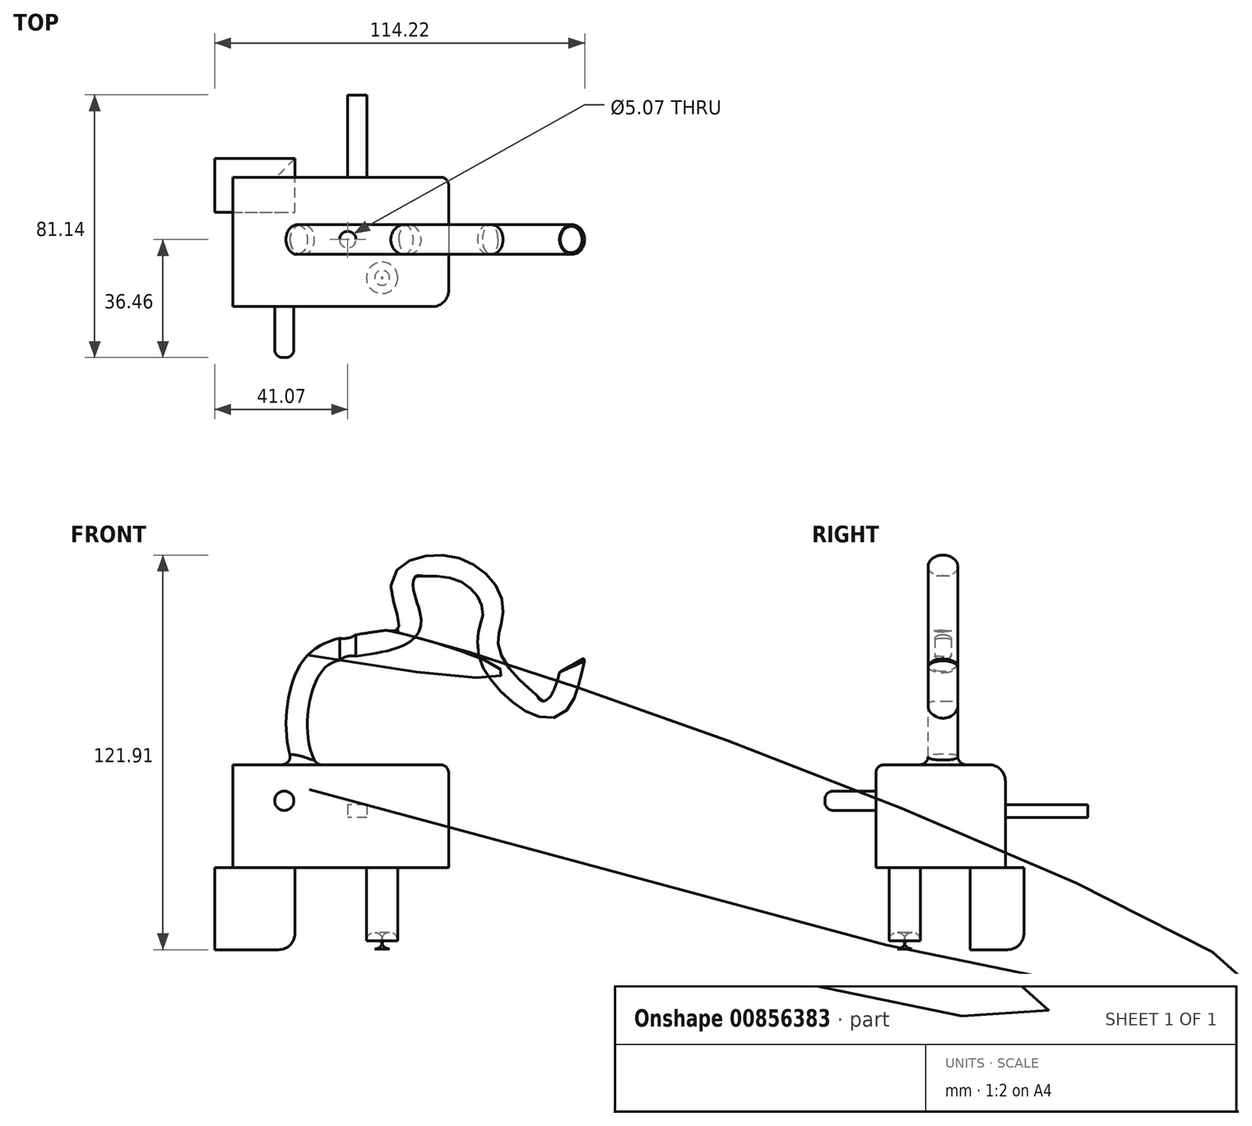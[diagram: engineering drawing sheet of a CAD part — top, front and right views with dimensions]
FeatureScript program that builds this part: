
annotation { "Feature Type Name" : "Feature", "Feature Type Description" : "" }
export const myFeature = defineFeature(function(context is Context, id is Id, definition is map)
    precondition{}
    {
        {
            var Q0;
            Q0=qCreatedBy(makeId("Top.planeOp"),FACE);
            var sketch = newSketch(context, id + "F0", { "sketchPlane" : qUnion([Q0])});
            skLineSegment(sketch, "E0.bottom", {"start": v(-35.49, 19.28) * mm, "end": v(31.16, 19.28) * mm});
            skLineSegment(sketch, "E0.top", {"start": v(-35.49, -20.72) * mm, "end": v(31.16, -20.72) * mm});
            skLineSegment(sketch, "E0.left", {"start": v(-35.49, 19.28) * mm, "end": v(-35.49, -20.72) * mm});
            skLineSegment(sketch, "E0.right", {"start": v(31.16, 19.28) * mm, "end": v(31.16, -20.72) * mm});
            skSolve(sketch);
        }
        {
            var Q0;
            Q0 = qSketchRegion(id + "F0", true);
            extrude(context, id + "F1", {"entities" : qUnion([Q0]), "depth" : 31.75 * mm, "offsetDistance" : 25.4 * mm});
        }
        {
            var Q0;
            Q0=makeQuery(id+"F1.opExtrude","SWEPT_FACE",FACE,{"disambiguationData":[OSD([sQuery(id+"F0.wireOp",EDGE,"E0.top")])]});
            var sketch = newSketch(context, id + "F2", { "sketchPlane" : qUnion([Q0])});
            skCircle(sketch, "E1", {"center": v(-19.62, 20.6) * mm, "radius": 2.98 * mm});
            skSolve(sketch);
        }
        {
            var Q0;
            Q0 = qSketchRegion(id + "F2", true);
            extrude(context, id + "F3", {"entities" : qUnion([Q0]), "operationType" : NewBodyOperationType.ADD, "depth" : 15.75 * mm, "offsetDistance" : 25.4 * mm});
        }
        {
            var Q0;
            Q0=makeQuery(id+"F1.opExtrude","SWEPT_EDGE",EDGE,{"disambiguationData":[OSD([sQuery(id+"F0.wireOp",EDGE,"E0.top"),sQuery(id+"F0.wireOp",EDGE,"E0.right")])]});
            fillet(context, id + "F4", {"entities" : qUnion([Q0]), "radius" : 5.08 * mm, "tangentPropagation" : true, "allowEdgeOverflow" : false});
        }
        {
            var Q0;
            Q0=makeQuery(id+"F1.opExtrude","CAP_FACE",FACE,{"disambiguationData":[OSD([sQuery(id+"F0.wireOp",EDGE,"E0.bottom"),sQuery(id+"F0.wireOp",EDGE,"E0.top"),sQuery(id+"F0.wireOp",EDGE,"E0.left"),sQuery(id+"F0.wireOp",EDGE,"E0.right")])],"isStart":true});
            var sketch = newSketch(context, id + "F5", { "sketchPlane" : qUnion([Q0])});
            skCircle(sketch, "E2", {"center": v(0, 0) * mm, "radius": 4.6 * mm});
            skSolve(sketch);
        }
        {
            var Q0;
            Q0=qCreatedBy(makeId("Front.planeOp"),FACE);
            var sketch = newSketch(context, id + "F6", { "sketchPlane" : qUnion([Q0])});
            skFitSpline(sketch, "E3", {"points": [v(0, 0) * mm, v(8.49, 13.84) * mm, v(-6.4, 24.07) * mm, v(-15.47, 40.82) * mm, v(-10.35, 62.45) * mm, v(5, 68.96) * mm, v(18.5, 74.78) * mm, v(17.56, 88.5) * mm, v(33.14, 92.22) * mm, v(44.3, 80.6) * mm, v(44.3, 65) * mm, v(61.98, 49.89) * mm, v(69.43, 62.68) * mm], "startDerivative": vector(179.85, 187.23) * mm, "endDerivative": vector(60.45, 239.3) * mm});
            skSolve(sketch);
        }
        {
            var Q0;
            Q0 = qSketchRegion(id + "F5", true);
            var Q1;
            Q1 = qConstructionFilter(qBodyType(qCreatedBy(id + "F6" ,EDGE), BodyType.WIRE), ConstructionObject.NO);
            sweep(context, id + "F7", {"operationType" : NewBodyOperationType.ADD, "profiles" : qUnion([Q0]), "path" : qUnion([Q1])});
        }
        {
            var Q0;
            Q0=makeQuery(id+"F1.opExtrude","SWEPT_FACE",FACE,{"disambiguationData":[OSD([sQuery(id+"F0.wireOp",EDGE,"E0.bottom")])]});
            var sketch = newSketch(context, id + "F8", { "sketchPlane" : qUnion([Q0])});
            skLineSegment(sketch, "E4.bottom", {"start": v(-5.84, 19.34) * mm, "end": v(0, 19.34) * mm});
            skLineSegment(sketch, "E4.top", {"start": v(-5.84, 15.39) * mm, "end": v(0, 15.39) * mm});
            skLineSegment(sketch, "E4.left", {"start": v(-5.84, 19.34) * mm, "end": v(-5.84, 15.39) * mm});
            skLineSegment(sketch, "E4.right", {"start": v(0, 19.34) * mm, "end": v(0, 15.39) * mm});
            skSolve(sketch);
        }
        {
            var Q0;
            Q0 = qSketchRegion(id + "F8", true);
            extrude(context, id + "F9", {"entities" : qUnion([Q0]), "operationType" : NewBodyOperationType.ADD, "depth" : 25.4 * mm, "offsetDistance" : 25.4 * mm});
        }
        {
            var Q0;
            Q0=makeQuery(id+"F1.opExtrude","CAP_EDGE",EDGE,{"disambiguationData":[OSD([sQuery(id+"F0.wireOp",EDGE,"E0.bottom")])],"isStart":false});
            fillet(context, id + "F10", {"entities" : qUnion([Q0]), "radius" : 5.08 * mm, "tangentPropagation" : true, "allowEdgeOverflow" : false});
        }
        {
            var Q0;
            Q0=makeQuery(id+"F7.opSweep","CAP_EDGE",EDGE,{"disambiguationData":[OSD([sQuery(id+"F5.wireOp",EDGE,"E2"),sQuery(id+"F6.wireOp",VERTEX,"E3.end")])],"isStart":false});
            fillet(context, id + "F11", {"entities" : qUnion([Q0]), "radius" : 0.5 * mm, "tangentPropagation" : true, "allowEdgeOverflow" : false});
        }
        {
            var Q0;
            Q0=makeQuery(id+"F1.opExtrude","CAP_FACE",FACE,{"disambiguationData":[OSD([sQuery(id+"F0.wireOp",EDGE,"E0.bottom"),sQuery(id+"F0.wireOp",EDGE,"E0.top"),sQuery(id+"F0.wireOp",EDGE,"E0.left"),sQuery(id+"F0.wireOp",EDGE,"E0.right")])],"isStart":true});
            var sketch = newSketch(context, id + "F12", { "sketchPlane" : qUnion([Q0])});
            skLineSegment(sketch, "E5.bottom", {"start": v(-41.07, -8.38) * mm, "end": v(-16.3, -8.38) * mm});
            skLineSegment(sketch, "E5.top", {"start": v(-41.07, -25.02) * mm, "end": v(-16.3, -25.02) * mm});
            skLineSegment(sketch, "E5.left", {"start": v(-41.07, -8.38) * mm, "end": v(-41.07, -25.02) * mm});
            skLineSegment(sketch, "E5.right", {"start": v(-16.3, -8.38) * mm, "end": v(-16.3, -25.02) * mm});
            skSolve(sketch);
        }
        {
            var Q0;
            Q0 = qSketchRegion(id + "F12", true);
            extrude(context, id + "F13", {"entities" : qUnion([Q0]), "operationType" : NewBodyOperationType.ADD, "depth" : 25.4 * mm, "offsetDistance" : 25.4 * mm});
        }
        {
            var Q0;
            Q0=qCreatedBy(makeId("Top.planeOp"),FACE);
            var sketch = newSketch(context, id + "F14", { "sketchPlane" : qUnion([Q0])});
            skCircle(sketch, "E6", {"center": v(10.6, -11.82) * mm, "radius": 4.84 * mm});
            skSolve(sketch);
        }
        {
            var Q0;
            Q0=makeQuery(id+"F14.imprint","IMPRINT",FACE,{"disambiguationData":[TD([[makeQuery(id+"F14.imprint","IMPRINT",EDGE,{"derivedFrom":sQuery(id+"F14.wireOp",EDGE,"E6")}),1.0]])]});
            extrude(context, id + "F15", {"entities" : qUnion([Q0]), "operationType" : NewBodyOperationType.ADD, "oppositeDirection" : true, "depth" : 25.15 * mm, "offsetDistance" : 25.4 * mm});
        }
        {
            var Q0;
            Q0=makeQuery(id+"F1.opExtrude","CAP_FACE",FACE,{"disambiguationData":[OSD([sQuery(id+"F0.wireOp",EDGE,"E0.bottom"),sQuery(id+"F0.wireOp",EDGE,"E0.top"),sQuery(id+"F0.wireOp",EDGE,"E0.left"),sQuery(id+"F0.wireOp",EDGE,"E0.right")])],"isStart":false});
            var sketch = newSketch(context, id + "F16", { "sketchPlane" : qUnion([Q0])});
            skCircle(sketch, "E7", {"center": v(0, 0) * mm, "radius": 2.54 * mm});
            skSolve(sketch);
        }
        {
            var Q0;
            Q0=makeQuery(id+"F16.imprint","IMPRINT",FACE,{"disambiguationData":[TD([[makeQuery(id+"F16.imprint","IMPRINT",EDGE,{"derivedFrom":sQuery(id+"F16.wireOp",EDGE,"E7")}),1.0]])]});
            extrude(context, id + "F17", {"entities" : qUnion([Q0]), "operationType" : NewBodyOperationType.REMOVE, "depth" : 69.1 * mm, "offsetDistance" : 25.4 * mm});
        }
        {
            var Q0;
            Q0=makeQuery(id+"F13.opExtrude","CAP_EDGE",EDGE,{"disambiguationData":[OSD([sQuery(id+"F12.wireOp",EDGE,"E5.top")])],"isStart":false});
            var Q1;
            Q1=makeQuery(id+"F13.opExtrude","CAP_EDGE",EDGE,{"disambiguationData":[OSD([sQuery(id+"F12.wireOp",EDGE,"E5.right")])],"isStart":false});
            fillet(context, id + "F18", {"entities" : qUnion([Q0, Q1]), "radius" : 5.08 * mm, "tangentPropagation" : true, "allowEdgeOverflow" : false});
        }
        {
            var Q0;
            Q0=makeQuery(id+"F7.boolean.opBoolean","INTERSECT",EDGE,{"derivedFrom":[makeQuery(id+"F1.opExtrude","CAP_FACE",FACE,{"disambiguationData":[OSD([sQuery(id+"F0.wireOp",EDGE,"E0.bottom"),sQuery(id+"F0.wireOp",EDGE,"E0.top"),sQuery(id+"F0.wireOp",EDGE,"E0.left"),sQuery(id+"F0.wireOp",EDGE,"E0.right")])],"isStart":false}),makeQuery(id+"F7.opSweep","SWEPT_FACE",FACE,{"disambiguationData":[OSD([sQuery(id+"F5.wireOp",EDGE,"E2"),sQuery(id+"F6.wireOp",EDGE,"E3")])]})]});
            var Q1;
            Q1=makeQuery(id+"F3.opExtrude","CAP_EDGE",EDGE,{"disambiguationData":[OSD([sQuery(id+"F2.wireOp",EDGE,"E1")])],"isStart":false});
            var Q2;
            Q2=makeQuery(id+"F15.opExtrude","CAP_EDGE",EDGE,{"disambiguationData":[OSD([sQuery(id+"F14.wireOp",EDGE,"E6")])],"isStart":false});
            var Q3;
            Q3=makeQuery(id+"F1.opExtrude","CAP_EDGE",EDGE,{"disambiguationData":[OSD([sQuery(id+"F0.wireOp",EDGE,"E0.right")])],"isStart":false});
            var Q4;
            Q4=makeQuery(id+"F1.opExtrude","SWEPT_EDGE",EDGE,{"disambiguationData":[OSD([sQuery(id+"F0.wireOp",EDGE,"E0.bottom"),sQuery(id+"F0.wireOp",EDGE,"E0.right")])]});
            var Q5;
            Q5=makeQuery(id+"F1.opExtrude","CAP_EDGE",EDGE,{"disambiguationData":[OSD([sQuery(id+"F0.wireOp",EDGE,"E0.top")])],"isStart":false});
            var Q6;
            Q6=makeQuery(id+"F3.opExtrude","CAP_EDGE",EDGE,{"disambiguationData":[OSD([sQuery(id+"F2.wireOp",EDGE,"E1")])],"isStart":true});
            var Q7;
            Q7=makeQuery(id+"F15.opExtrude","CAP_EDGE",EDGE,{"disambiguationData":[OSD([sQuery(id+"F14.wireOp",EDGE,"E6")])],"isStart":true});
            fillet(context, id + "F19", {"entities" : qUnion([Q0, Q1, Q2, Q3, Q4, Q5, Q6, Q7]), "radius" : 2.54 * mm, "tangentPropagation" : true, "allowEdgeOverflow" : false});
        }
    });
